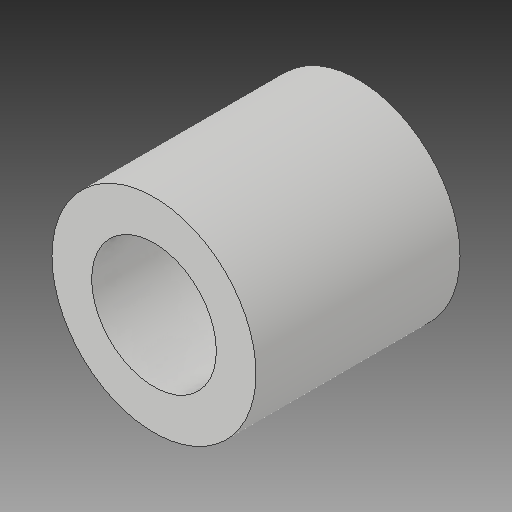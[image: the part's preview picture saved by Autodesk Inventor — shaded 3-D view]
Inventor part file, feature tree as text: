
AUTODESK INVENTOR PART (.ipt)
format: ipt  version: 2018 (Build 220112000, 112)  size: 102,400 bytes
history: native  units: mm
features: extrude x1, sketch x1
ambient origin geometry x8: Origin, YZ Plane, XZ Plane, XY Plane, X Axis, Y Axis, Z Axis, Center Point
bodies: Solid1 (feature_tree)
feature tree (2):
  extrude  "Extrusion1"  Depth=9.0mm
  sketch  "Sketch1"  dims[d0=5.5mm d1=9.0mm d2=9.0mm d3=0.0mm]
